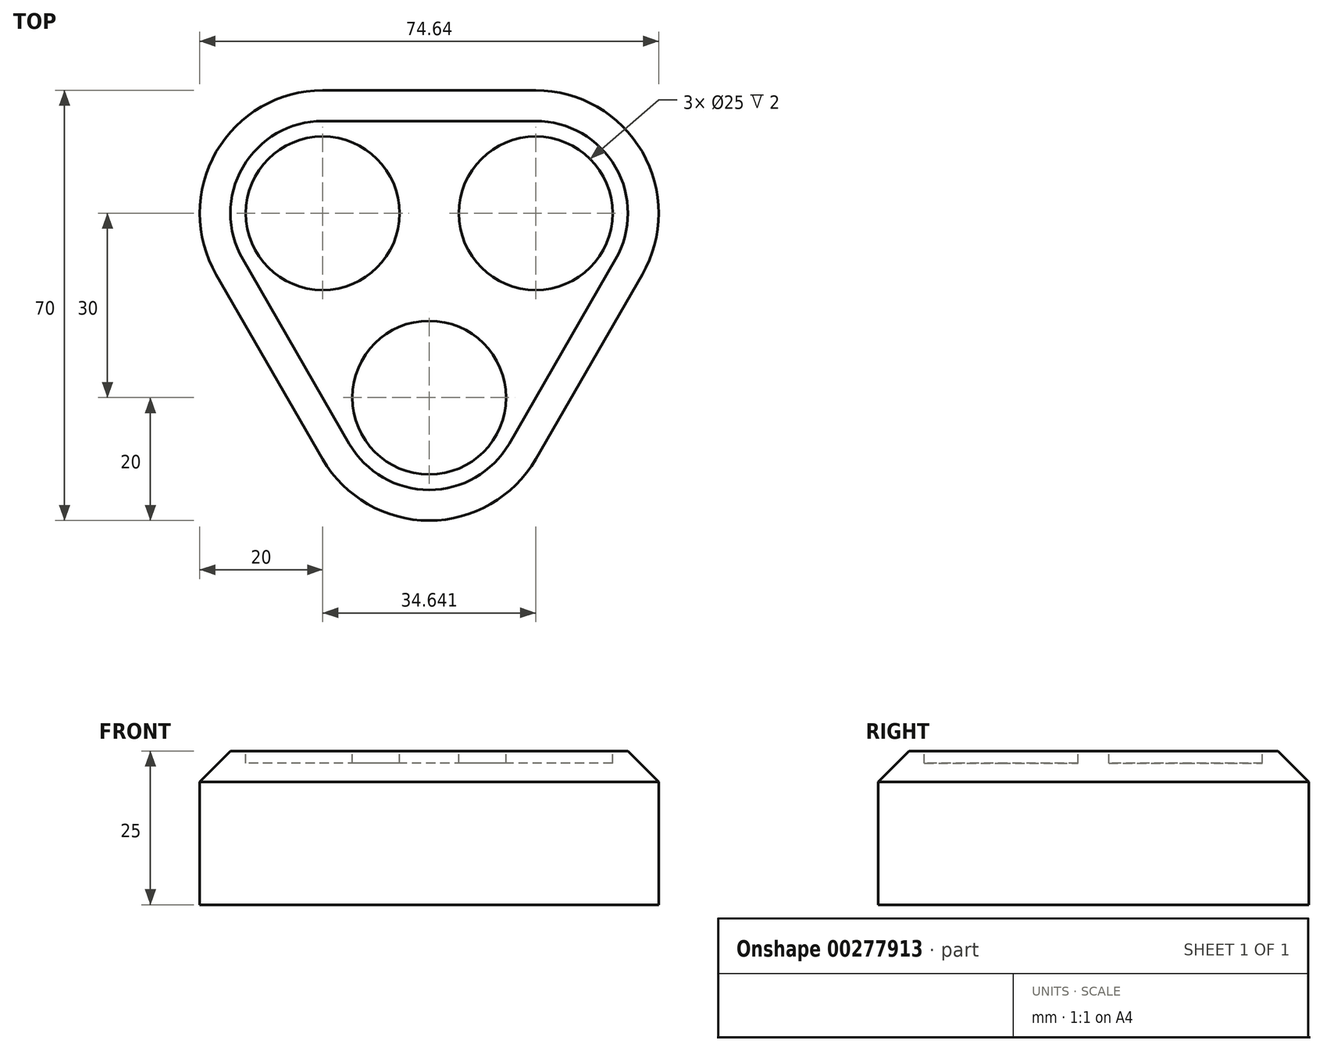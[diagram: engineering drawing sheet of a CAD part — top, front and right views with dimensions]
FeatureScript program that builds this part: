
annotation { "Feature Type Name" : "Feature", "Feature Type Description" : "" }
export const myFeature = defineFeature(function(context is Context, id is Id, definition is map)
    precondition{}
    {
        {
            var Q0;
            Q0=qCreatedBy(makeId("Top.planeOp"),FACE);
            var sketch = newSketch(context, id + "F0", { "sketchPlane" : qUnion([Q0])});
            skCircle(sketch, "E0.cCircle", {"center": v(0, 0) * mm, "radius": 30 * mm, "construction": true});
            skLineSegment(sketch, "E0.0", {"start": v(-17.32, 30) * mm, "end": v(17.32, 30) * mm});
            skLineSegment(sketch, "E0.1", {"start": v(34.64, 0) * mm, "end": v(17.32, -30) * mm});
            skLineSegment(sketch, "E0.2", {"start": v(-17.32, -30) * mm, "end": v(-34.64, 0) * mm});
            skPoint(sketch, "E0.0.midPoint", {"position": v(0, 30) * mm});
            skLineSegment(sketch, "E1", {"start": v(0, 0) * mm, "end": v(-51.96, 30) * mm, "construction": true});
            skCircle(sketch, "E2", {"center": v(-17.32, 10) * mm, "radius": 12.5 * mm, "construction": true});
            skCircle(sketch, "E3.1.0", {"center": v(0, -20) * mm, "radius": 12.5 * mm, "construction": true});
            skCircle(sketch, "E3.2.0", {"center": v(17.32, 10) * mm, "radius": 12.5 * mm, "construction": true});
            skLineSegment(sketch, "E4", {"start": v(-17.32, 10) * mm, "end": v(-17.32, 30) * mm, "construction": true});
            skPoint(sketch, "E5.visualSharp", {"position": v(-51.96, 30) * mm});
            skArc(sketch, "E5.filletArc", {"start": v(-17.32, 30) * mm, "mid": v(-34.64, 20) * mm, "end": v(-34.64, 0) * mm});
            skPoint(sketch, "E6.visualSharp", {"position": v(0, -60) * mm});
            skArc(sketch, "E6.filletArc", {"start": v(-17.32, -30) * mm, "mid": v(0, -40) * mm, "end": v(17.32, -30) * mm});
            skPoint(sketch, "E7.visualSharp", {"position": v(51.96, 30) * mm});
            skArc(sketch, "E7.filletArc", {"start": v(34.64, 0) * mm, "mid": v(34.64, 20) * mm, "end": v(17.32, 30) * mm});
            skSolve(sketch);
        }
        {
            var Q0;
            Q0=qSketchRegion(id+"F0",true);
            extrude(context, id + "F1", {"entities" : qUnion([Q0]), "depth" : 25 * mm});
        }
        {
            var Q0;
            Q0=makeQuery(id+"F1.opExtrude","CAP_FACE",FACE,{"disambiguationData":[OSD([sQuery(id+"F0.wireOp",EDGE,"E0.0"),sQuery(id+"F0.wireOp",EDGE,"E0.1"),sQuery(id+"F0.wireOp",EDGE,"E0.2"),sQuery(id+"F0.wireOp",EDGE,"E5.filletArc"),sQuery(id+"F0.wireOp",EDGE,"E6.filletArc"),sQuery(id+"F0.wireOp",EDGE,"E7.filletArc")])],"isStart":false});
            var sketch = newSketch(context, id + "F2", { "sketchPlane" : qUnion([Q0])});
            skLineSegment(sketch, "E8", {"start": v(0, 0) * mm, "end": v(-34.64, 20) * mm, "construction": true});
            skCircle(sketch, "E9", {"center": v(-17.32, 10) * mm, "radius": 12.5 * mm});
            skCircle(sketch, "E10.1.0", {"center": v(0, -20) * mm, "radius": 12.5 * mm});
            skCircle(sketch, "E10.2.0", {"center": v(17.32, 10) * mm, "radius": 12.5 * mm});
            skPoint(sketch, "E10.center", {"position": v(0, 0) * mm});
            skSolve(sketch);
        }
        {
            var Q0;
            Q0=qSketchRegion(id+"F2",true);
            extrude(context, id + "F3", {"entities" : qUnion([Q0]), "operationType" : NewBodyOperationType.REMOVE, "oppositeDirection" : true, "depth" : 2 * mm});
        }
        {
            var Q0;
            Q0=makeQuery(id+"F1.opExtrude","CAP_EDGE",EDGE,{"disambiguationData":[OSD([sQuery(id+"F0.wireOp",EDGE,"E0.1")])],"isStart":false});
            chamfer(context, id + "F4", {"entities" : qUnion([Q0]), "width" : 5 * mm, "tangentPropagation" : true});
        }
    });
